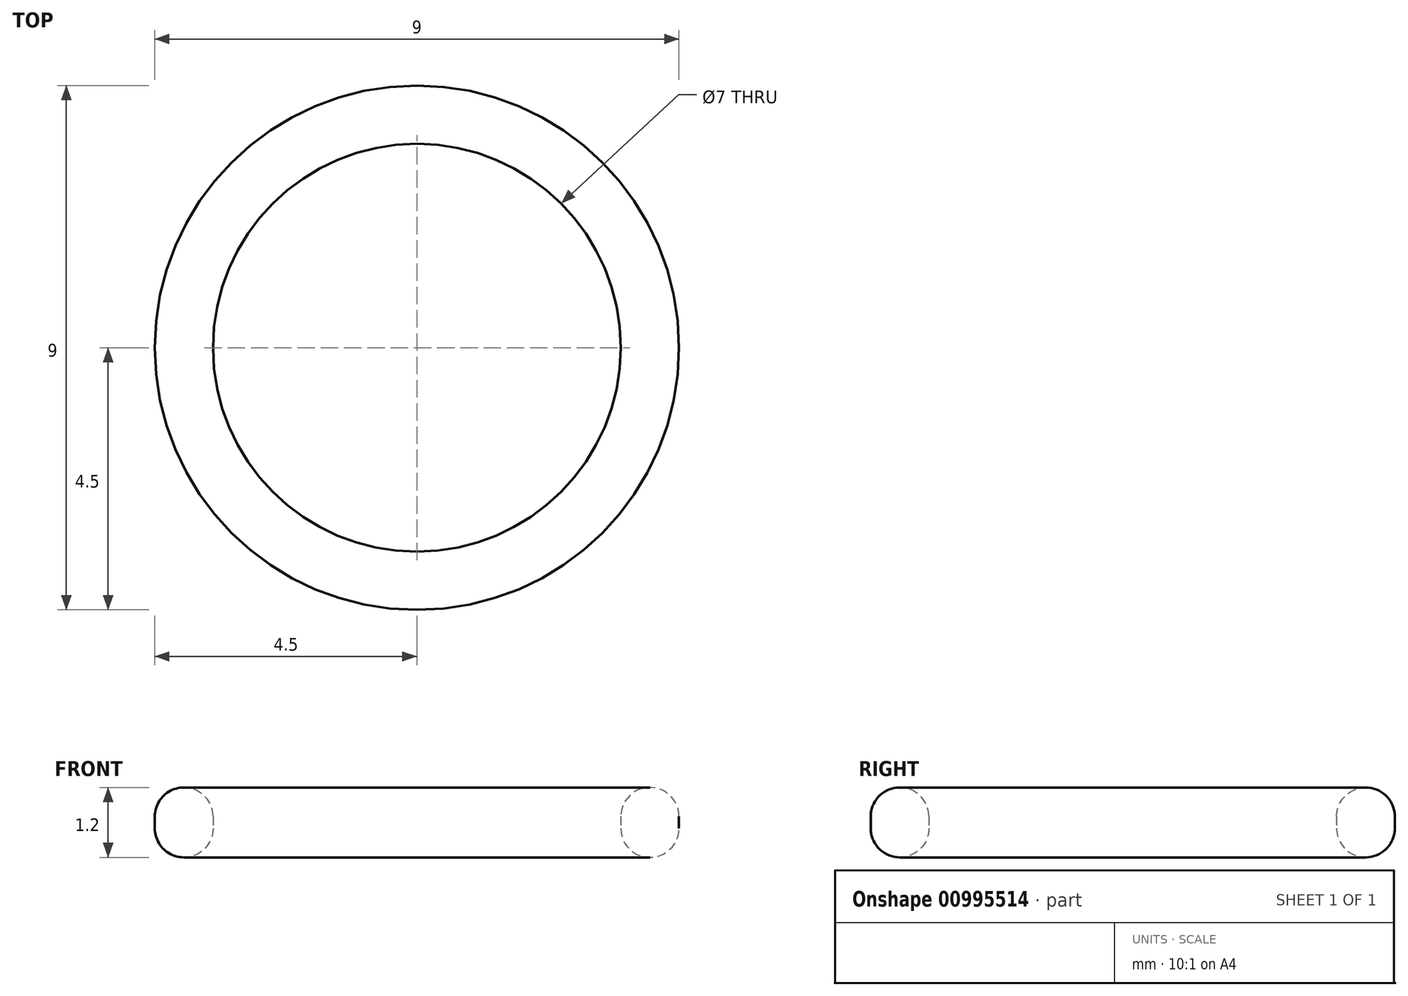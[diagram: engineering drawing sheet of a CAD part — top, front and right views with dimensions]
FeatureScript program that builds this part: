
annotation { "Feature Type Name" : "Feature", "Feature Type Description" : "" }
export const myFeature = defineFeature(function(context is Context, id is Id, definition is map)
    precondition{}
    {
        {
            var Q0;
            Q0=qCreatedBy(makeId("Top.planeOp"),FACE);
            var sketch = newSketch(context, id + "F0", { "sketchPlane" : qUnion([Q0])});
            skCircle(sketch, "E0", {"center": v(0, 0) * mm, "radius": 3.5 * mm});
            skCircle(sketch, "E1", {"center": v(0, 0) * mm, "radius": 4.5 * mm});
            skSolve(sketch);
        }
        {
            var Q0;
            Q0=makeQuery(id+"F0.imprint","IMPRINT",FACE,{"disambiguationData":[TD([[makeQuery(id+"F0.imprint","IMPRINT",EDGE,{"derivedFrom":sQuery(id+"F0.wireOp",EDGE,"E0")}),-1.0]])]});
            extrude(context, id + "F1", {"entities" : qUnion([Q0]), "depth" : 1.2 * mm, "offsetDistance" : 25 * mm});
        }
        {
            var Q0;
            Q0=makeQuery(id+"F1.opExtrude","CAP_EDGE",EDGE,{"disambiguationData":[OSD([sQuery(id+"F0.wireOp",EDGE,"E1")])],"isStart":false});
            var Q1;
            Q1=makeQuery(id+"F1.opExtrude","CAP_EDGE",EDGE,{"disambiguationData":[OSD([sQuery(id+"F0.wireOp",EDGE,"E1")])],"isStart":true});
            var Q2;
            Q2=makeQuery(id+"F1.opExtrude","CAP_EDGE",EDGE,{"disambiguationData":[OSD([sQuery(id+"F0.wireOp",EDGE,"E0")])],"isStart":true});
            var Q3;
            Q3=makeQuery(id+"F1.opExtrude","CAP_EDGE",EDGE,{"disambiguationData":[OSD([sQuery(id+"F0.wireOp",EDGE,"E0")])],"isStart":false});
            fillet(context, id + "F2", {"entities" : qUnion([Q0, Q1, Q2, Q3]), "radius" : .5 * mm, "tangentPropagation" : true, "allowEdgeOverflow" : false});
        }
    });
